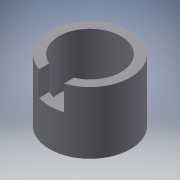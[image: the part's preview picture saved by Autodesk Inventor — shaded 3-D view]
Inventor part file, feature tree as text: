
AUTODESK INVENTOR PART (.ipt)
format: ipt  version: 2016 (Build 200138000, 138)  size: 104,960 bytes
history: native  units: mm
features: extrude x3, sketch x3, projected_geometry x1
ambient origin geometry x8: Origin, YZ Plane, XZ Plane, XY Plane, X Axis, Y Axis, Z Axis, Center Point
bodies: Solid1 (feature_tree)
feature tree (7):
  extrude  "Extrusion1"  Depth=10.0mm TaperAngle=0.0deg
  extrude  "Extrusion2"  Depth=8.0mm TaperAngle=0.0deg
  extrude  "Extrusion3"  Depth=4.0mm TaperAngle=0.0deg
  sketch  "Sketch1"  dims[d0=13.0mm d1=10.0mm d2=0.0mm]
  sketch  "Sketch2"  dims[d3=10.0mm d4=8.0mm d5=0.0mm]
  sketch  "Sketch3"  dims[d6=4.0mm d7=4.0mm d8=0.0mm]
  projected_geometry  "Projected Loop1"
